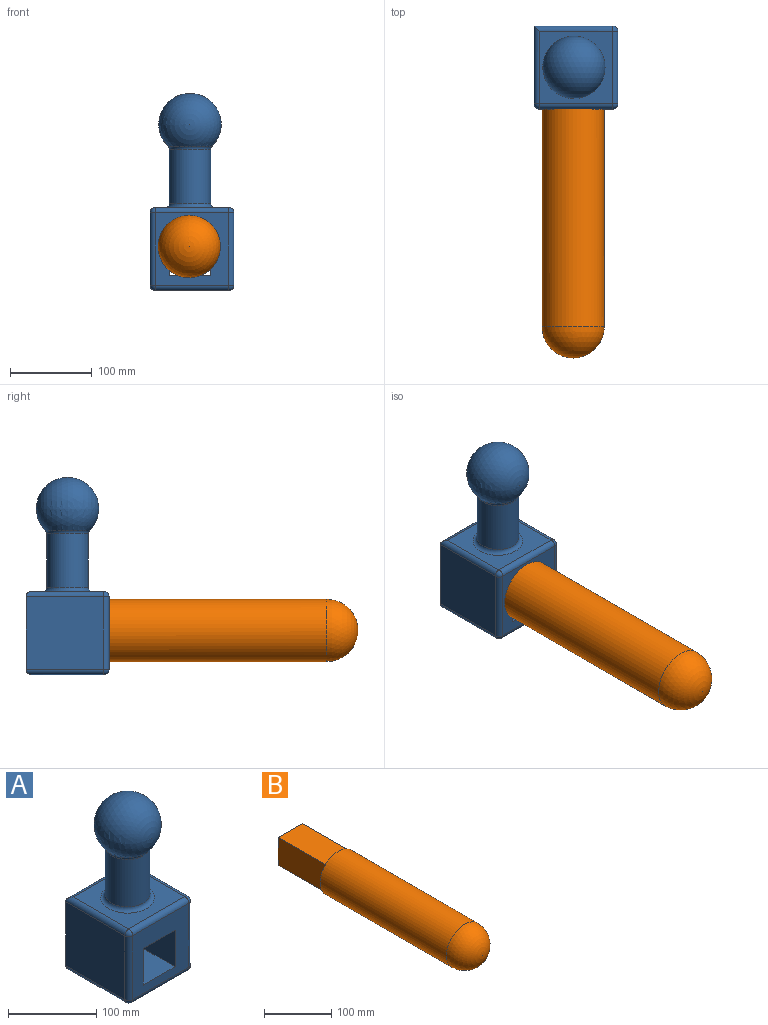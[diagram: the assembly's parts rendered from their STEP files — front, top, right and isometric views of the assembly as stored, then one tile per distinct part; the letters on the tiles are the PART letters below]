
ASSEMBLY  parts=2 mates=1
PART A: 33 faces, bbox 102.8x101.6x241.4 mm
  f0: cylinder r=25.4mm len=65.81mm, axis (0,0,-1), area 10502.9mm2, adj f29,f30
  f1: plane 96.42x88.9mm, normal (0,1,0), area 5991mm2, adj f2,f8,f9,f10,f11,f12,f18,f21
  f2: plane 95.25x88.9mm, normal (-1,0,0), area 8467.7mm2, adj f1,f22,f25,f28
  f3: plane 90.07x88.9mm, normal (0,-1,0), area 5426.4mm2, adj f8,f9,f10,f11,f15,f23,f24,f28
  f4: plane 88.9x88.9mm, normal (1,0,0), area 7903.2mm2, adj f12,f14,f15,f16
  f5: plane 90.07x88.9mm, normal (0,0,1), area 5088.4mm2, adj f14,f18,f22,f23,f30
  f6: plane 90.07x88.9mm, normal (0,0,-1), area 8007.1mm2, adj f16,f21,f24,f25
  f7: sphere r=38.19mm, area 15665.7mm2, adj f29
  f8: plane 101.6x50.8mm, normal (1,0,0), area 5161.3mm2, adj f1,f3,f9,f11
  f9: plane 101.6x50.8mm, normal (0,0,1), area 5161.3mm2, adj f1,f3,f8,f10
  f10: plane 101.6x50.8mm, normal (-1,0,0), area 5161.3mm2, adj f1,f3,f9,f11
  f11: plane 101.6x50.8mm, normal (0,0,-1), area 5161.3mm2, adj f1,f3,f8,f10
  f12: cylinder r=6.35mm len=88.9mm, axis (0,0,1), area 886.7mm2, adj f1,f4,f13,f17
  f13: sphere r=6.35mm, area 63.3mm2, adj f12,f14,f18
  f14: cylinder r=6.35mm len=88.9mm, axis (0,-1,0), area 886.7mm2, adj f4,f5,f13,f19
  f15: cylinder r=6.35mm len=88.9mm, axis (0,0,-1), area 886.7mm2, adj f3,f4,f19,f20
  f16: cylinder r=6.35mm len=88.9mm, axis (0,1,0), area 886.7mm2, adj f4,f6,f17,f20
  f17: sphere r=6.35mm, area 63.3mm2, adj f12,f16,f21
  f18: cylinder r=6.35mm len=96.42mm, axis (1,0,0), area 938.7mm2, adj f1,f5,f13,f22
  f19: sphere r=6.35mm, area 63.3mm2, adj f14,f15,f23
  f20: sphere r=6.35mm, area 63.3mm2, adj f15,f16,f24
  f21: cylinder r=6.35mm len=96.42mm, axis (-1,0,0), area 938.7mm2, adj f1,f6,f17,f25
  f22: cylinder r=6.35mm len=95.25mm, axis (0,1,0), area 927.1mm2, adj f2,f5,f18,f26
  f23: cylinder r=6.35mm len=90.07mm, axis (-1,0,0), area 898.4mm2, adj f3,f5,f19,f26
  f24: cylinder r=6.35mm len=90.07mm, axis (1,0,0), area 898.4mm2, adj f3,f6,f20,f27
  f25: cylinder r=6.35mm len=95.25mm, axis (0,-1,0), area 927.1mm2, adj f2,f6,f21,f27
  f26: sphere r=6.35mm, area 63.3mm2, adj f22,f23,f28
  f27: sphere r=6.35mm, area 63.3mm2, adj f24,f25,f28
  f28: cylinder r=6.35mm len=88.9mm, axis (0,0,1), area 886.7mm2, adj f2,f3,f26,f27
  f29: torus R=30.48mm, axis (0,0,1), area 652.7mm2, adj f0,f7
  f30: torus R=30.48mm, axis (0,0,1), area 1366mm2, adj f0,f5
  f31: sphere r=25.4mm, area 4053.7mm2, adj f32
  f32: plane 50.8x50.8mm, normal (0,0,1), area 2026.8mm2, adj f31
PART B: 8 faces, bbox 76.2x406.4x76.2 mm
  f0: plane 101.6x50.8mm, normal (1,0,0), area 5161.3mm2, adj f1,f3,f4,f5
  f1: plane 101.6x50.8mm, normal (0,0,1), area 5161.3mm2, adj f0,f2,f4,f5
  f2: plane 101.6x50.8mm, normal (-1,0,0), area 5161.3mm2, adj f1,f3,f4,f5
  f3: plane 101.6x50.8mm, normal (0,0,-1), area 5161.3mm2, adj f0,f2,f4,f5
  f4: plane 50.8x50.8mm, normal (0,1,0), area 2580.6mm2, adj f0,f1,f2,f3
  f5: plane 76.2x76.2mm, normal (0,1,0), area 1979.7mm2, adj f0,f1,f2,f3,f6
  f6: cylinder r=38.1mm len=266.7mm, axis (0,1,0), area 63845.1mm2, adj f5,f7
  f7: sphere r=38.1mm, area 9120.7mm2, adj f6
PLACE A t=(-7.48,72.95,-6.93)mm fixed
PLACE B t=(-8.48,123.75,46.98)mm
MATE fastened B.f6 <-> A.f1  axis (0,1,0) through (-8.48,123.75,46.98)mm
